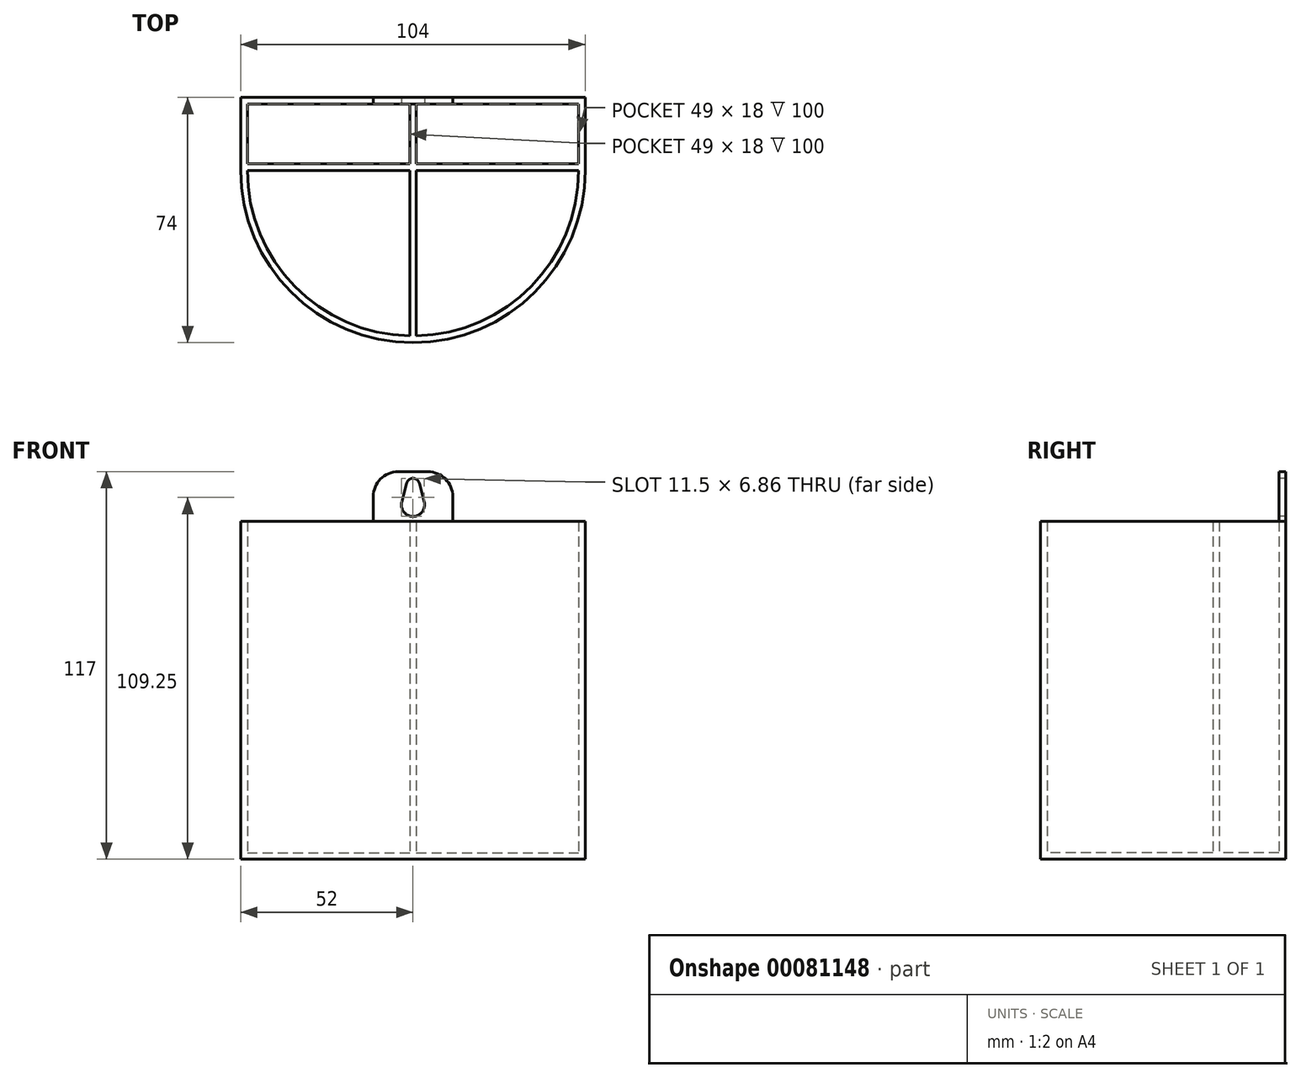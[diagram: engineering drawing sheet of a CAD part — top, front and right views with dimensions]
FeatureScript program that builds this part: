
annotation { "Feature Type Name" : "Feature", "Feature Type Description" : "" }
export const myFeature = defineFeature(function(context is Context, id is Id, definition is map)
    precondition{}
    {
        {
            var Q0;
            Q0=qCreatedBy(makeId("Top.planeOp"),FACE);
            var sketch = newSketch(context, id + "F0", { "sketchPlane" : qUnion([Q0])});
            skLineSegment(sketch, "E0", {"start": v(0, 0) * mm, "end": v(104, 0) * mm});
            skLineSegment(sketch, "E1", {"start": v(0, 0) * mm, "end": v(0, -22) * mm});
            skLineSegment(sketch, "E2", {"start": v(104, 0) * mm, "end": v(104, -22) * mm});
            skArc(sketch, "E3", {"start": v(0, -22) * mm, "mid": v(52, -74) * mm, "end": v(104, -22) * mm});
            skSolve(sketch);
        }
        {
            var Q0;
            Q0 = qSketchRegion(id + "F0", true);
            extrude(context, id + "F1", {"entities" : qUnion([Q0]), "depth" : 2 * mm});
        }
        {
            var Q0;
            Q0=makeQuery(id+"F1.opExtrude","CAP_FACE",FACE,{"disambiguationData":[OSD([sQuery(id+"F0.wireOp",EDGE,"E0"),sQuery(id+"F0.wireOp",EDGE,"E1"),sQuery(id+"F0.wireOp",EDGE,"E2"),sQuery(id+"F0.wireOp",EDGE,"E3")])],"isStart":false});
            var sketch = newSketch(context, id + "F2", { "sketchPlane" : qUnion([Q0])});
            skLineSegment(sketch, "E4.0", {"start": v(0, 0) * mm, "end": v(0, -22) * mm});
            skLineSegment(sketch, "E4.1", {"start": v(0, 0) * mm, "end": v(104, 0) * mm});
            skLineSegment(sketch, "E4.2", {"start": v(104, 0) * mm, "end": v(104, -22) * mm});
            skArc(sketch, "E4.3", {"start": v(0, -22) * mm, "mid": v(52, -74) * mm, "end": v(104, -22) * mm});
            skLineSegment(sketch, "E5.0", {"start": v(2, -2) * mm, "end": v(2, -20) * mm});
            skLineSegment(sketch, "E5.1", {"start": v(2, -2) * mm, "end": v(51, -2) * mm});
            skLineSegment(sketch, "E5.2", {"start": v(102, -2) * mm, "end": v(102, -20) * mm});
            skArc(sketch, "E5.3", {"start": v(2, -22) * mm, "mid": v(16.3, -57) * mm, "end": v(51, -71.99) * mm});
            skLineSegment(sketch, "E6", {"start": v(52, -2) * mm, "end": v(52, -72) * mm, "construction": true});
            skLineSegment(sketch, "E7", {"start": v(51, -2) * mm, "end": v(51, -20) * mm});
            skLineSegment(sketch, "E8", {"start": v(53, -2) * mm, "end": v(53, -20) * mm});
            skLineSegment(sketch, "E9.trimOffspring", {"start": v(53, -2) * mm, "end": v(102, -2) * mm});
            skArc(sketch, "E10.trimOffspring", {"start": v(53, -71.99) * mm, "mid": v(87.7, -57) * mm, "end": v(102, -22) * mm});
            skLineSegment(sketch, "E11", {"start": v(2, -22) * mm, "end": v(51, -22) * mm});
            skLineSegment(sketch, "E12", {"start": v(2, -20) * mm, "end": v(51, -20) * mm});
            skLineSegment(sketch, "E13", {"start": v(53, -22) * mm, "end": v(102, -22) * mm});
            skLineSegment(sketch, "E14", {"start": v(53, -20) * mm, "end": v(102, -20) * mm});
            skLineSegment(sketch, "E15.trimOffspring", {"start": v(53, -22) * mm, "end": v(53, -71.99) * mm});
            skLineSegment(sketch, "E16.trimOffspring", {"start": v(51, -22) * mm, "end": v(51, -71.99) * mm});
            skSolve(sketch);
        }
        {
            var Q0;
            Q0 = qSketchRegion(id + "F2", true);
            extrude(context, id + "F3", {"entities" : qUnion([Q0]), "operationType" : NewBodyOperationType.ADD, "depth" : 100 * mm});
        }
        {
            var Q0;
            Q0=makeQuery(id+"F3.opExtrude","CAP_FACE",FACE,{"disambiguationData":[OSD([sQuery(id+"F2.wireOp",EDGE,"E4.0"),sQuery(id+"F2.wireOp",EDGE,"E4.1"),sQuery(id+"F2.wireOp",EDGE,"E4.2"),sQuery(id+"F2.wireOp",EDGE,"E4.3"),sQuery(id+"F2.wireOp",EDGE,"E5.0"),sQuery(id+"F2.wireOp",EDGE,"E5.1"),sQuery(id+"F2.wireOp",EDGE,"E5.2"),sQuery(id+"F2.wireOp",EDGE,"E5.3"),sQuery(id+"F2.wireOp",EDGE,"E7"),sQuery(id+"F2.wireOp",EDGE,"E8"),sQuery(id+"F2.wireOp",EDGE,"E9.trimOffspring"),sQuery(id+"F2.wireOp",EDGE,"E10.trimOffspring"),sQuery(id+"F2.wireOp",EDGE,"E11"),sQuery(id+"F2.wireOp",EDGE,"E12"),sQuery(id+"F2.wireOp",EDGE,"E13"),sQuery(id+"F2.wireOp",EDGE,"E14"),sQuery(id+"F2.wireOp",EDGE,"E15.trimOffspring"),sQuery(id+"F2.wireOp",EDGE,"E16.trimOffspring")])],"isStart":false});
            var sketch = newSketch(context, id + "F4", { "sketchPlane" : qUnion([Q0])});
            skLineSegment(sketch, "E17.bottom", {"start": v(40, 0) * mm, "end": v(64, 0) * mm});
            skLineSegment(sketch, "E17.top", {"start": v(40, -2) * mm, "end": v(64, -2) * mm});
            skLineSegment(sketch, "E17.left", {"start": v(40, 0) * mm, "end": v(40, -2) * mm});
            skLineSegment(sketch, "E17.right", {"start": v(64, 0) * mm, "end": v(64, -2) * mm});
            skSolve(sketch);
        }
        {
            var Q0;
            Q0 = qSketchRegion(id + "F4", true);
            extrude(context, id + "F5", {"entities" : qUnion([Q0]), "operationType" : NewBodyOperationType.ADD, "depth" : 15 * mm});
        }
        {
            var Q0;
            Q0=makeQuery(id+"F5.boolean.opBoolean","MERGE",FACE,{"derivedFrom":[makeQuery(id+"F3.opExtrude","SWEPT_FACE",FACE,{"disambiguationData":[OSD([sQuery(id+"F2.wireOp",EDGE,"E5.1")])]}),makeQuery(id+"F3.opExtrude","SWEPT_FACE",FACE,{"disambiguationData":[OSD([sQuery(id+"F2.wireOp",EDGE,"E9.trimOffspring")])]}),makeQuery(id+"F5.opExtrude","SWEPT_FACE",FACE,{"disambiguationData":[OSD([sQuery(id+"F4.wireOp",EDGE,"E17.top")])]})]});
            var sketch = newSketch(context, id + "F6", { "sketchPlane" : qUnion([Q0])});
            skLineSegment(sketch, "E18", {"start": v(52, 117) * mm, "end": v(52, 102) * mm, "construction": true});
            skArc(sketch, "E19", {"start": v(53.94, 113.5) * mm, "mid": v(52, 115) * mm, "end": v(50.06, 113.5) * mm});
            skArc(sketch, "E20", {"start": v(48.61, 107.88) * mm, "mid": v(52, 103.5) * mm, "end": v(55.39, 107.88) * mm});
            skLineSegment(sketch, "E21", {"start": v(50.06, 113.5) * mm, "end": v(48.61, 107.88) * mm});
            skLineSegment(sketch, "E22", {"start": v(53.94, 113.5) * mm, "end": v(55.39, 107.88) * mm});
            skSolve(sketch);
        }
        {
            var Q0;
            Q0 = qSketchRegion(id + "F6", true);
            var Q1;
            Q1=makeQuery(id+"F5.boolean.opBoolean","MERGE",FACE,{"derivedFrom":[makeQuery(id+"F3.boolean.opBoolean","MERGE",FACE,{"derivedFrom":[makeQuery(id+"F1.opExtrude","SWEPT_FACE",FACE,{"disambiguationData":[OSD([sQuery(id+"F0.wireOp",EDGE,"E0")])]}),makeQuery(id+"F3.opExtrude","SWEPT_FACE",FACE,{"disambiguationData":[OSD([sQuery(id+"F2.wireOp",EDGE,"E4.1")])]})]}),makeQuery(id+"F5.opExtrude","SWEPT_FACE",FACE,{"disambiguationData":[OSD([sQuery(id+"F4.wireOp",EDGE,"E17.bottom")])]})]});
            extrude(context, id + "F7", {"entities" : qUnion([Q0]), "operationType" : NewBodyOperationType.REMOVE, "endBound" : BoundingType.UP_TO_SURFACE, "oppositeDirection" : true, "endBoundEntityFace" : qUnion([Q1]), "depth" : 25 * mm});
        }
        {
            var Q0;
            Q0=makeQuery(id+"F5.opExtrude","CAP_EDGE",EDGE,{"disambiguationData":[OSD([sQuery(id+"F4.wireOp",EDGE,"E17.right")])],"isStart":true});
            var Q1;
            Q1=makeQuery(id+"F5.opExtrude","CAP_EDGE",EDGE,{"disambiguationData":[OSD([sQuery(id+"F4.wireOp",EDGE,"E17.right")])],"isStart":false});
            var Q2;
            Q2=makeQuery(id+"F5.opExtrude","CAP_EDGE",EDGE,{"disambiguationData":[OSD([sQuery(id+"F4.wireOp",EDGE,"E17.left")])],"isStart":true});
            var Q3;
            Q3=makeQuery(id+"F5.opExtrude","CAP_EDGE",EDGE,{"disambiguationData":[OSD([sQuery(id+"F4.wireOp",EDGE,"E17.left")])],"isStart":false});
            fillet(context, id + "F8", {"entities" : qUnion([Q0, Q1, Q2, Q3]), "radius" : 7.5 * mm, "tangentPropagation" : true, "allowEdgeOverflow" : false});
        }
    });
